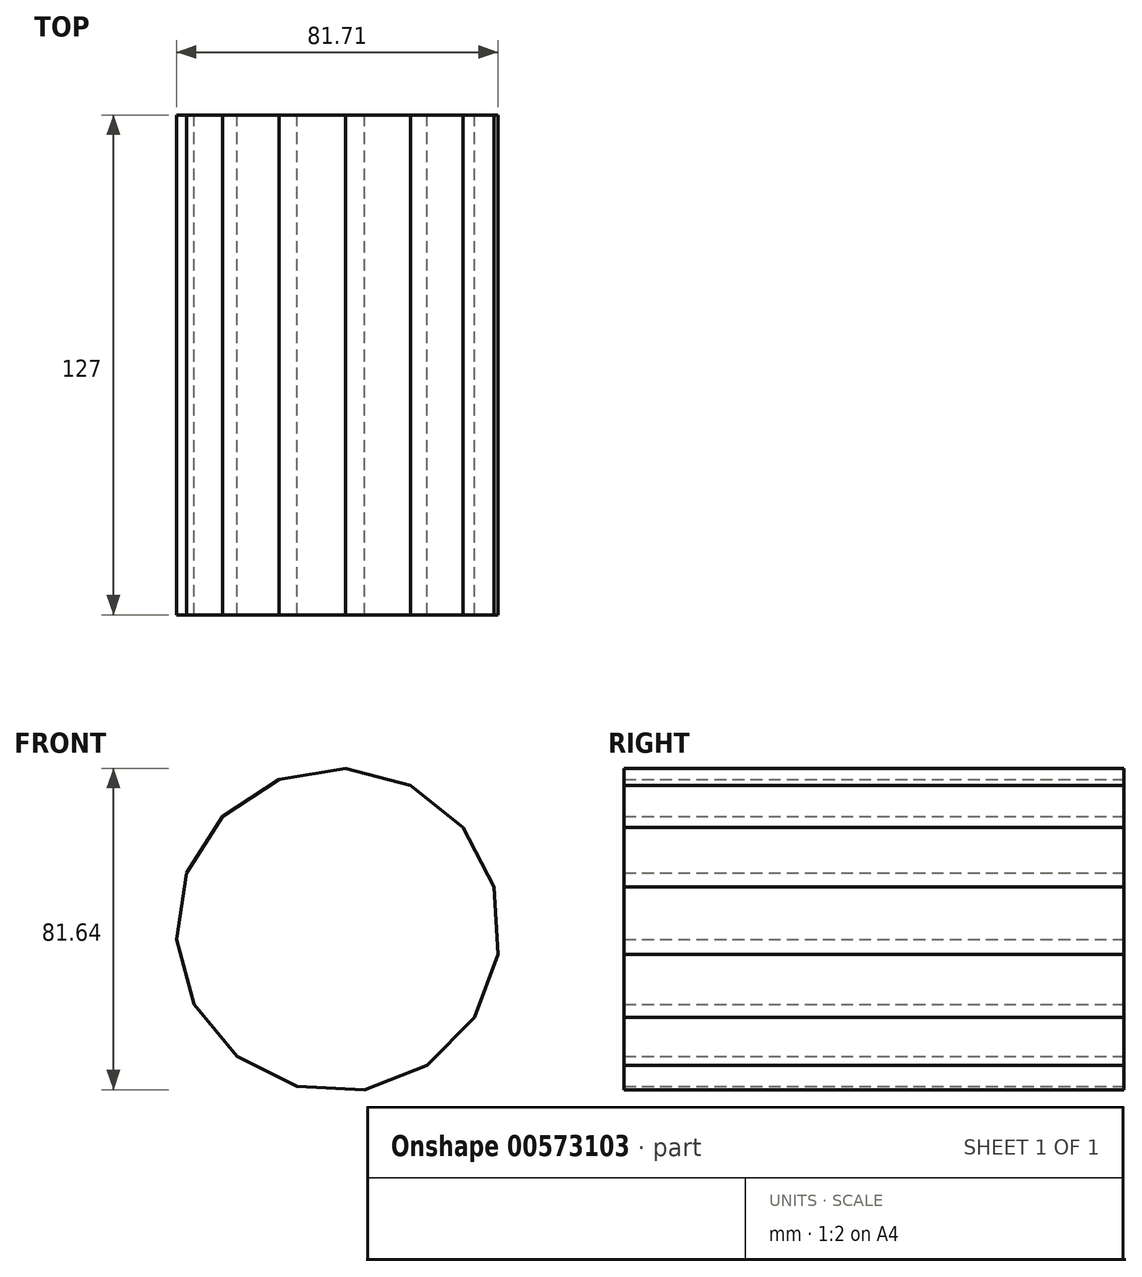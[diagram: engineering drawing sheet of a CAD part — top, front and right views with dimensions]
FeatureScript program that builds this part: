
annotation { "Feature Type Name" : "Feature", "Feature Type Description" : "" }
export const myFeature = defineFeature(function(context is Context, id is Id, definition is map)
    precondition{}
    {
        {
            var Q0;
            Q0=qCreatedBy(makeId("Front.planeOp"),FACE);
            var sketch = newSketch(context, id + "F0", { "sketchPlane" : qUnion([Q0])});
            skCircle(sketch, "E0.cCircle", {"center": v(-0.12, -0.11) * mm, "radius": 40.22 * mm, "construction": true});
            skLineSegment(sketch, "E0.0", {"start": v(34.51, -22.28) * mm, "end": v(22.5, -34.45) * mm});
            skLineSegment(sketch, "E0.1", {"start": v(22.5, -34.45) * mm, "end": v(6.58, -40.68) * mm});
            skLineSegment(sketch, "E0.2", {"start": v(6.58, -40.68) * mm, "end": v(-10.5, -39.9) * mm});
            skLineSegment(sketch, "E0.3", {"start": v(-10.5, -39.9) * mm, "end": v(-25.78, -32.24) * mm});
            skLineSegment(sketch, "E0.4", {"start": v(-25.78, -32.24) * mm, "end": v(-36.63, -19.03) * mm});
            skLineSegment(sketch, "E0.5", {"start": v(-36.63, -19.03) * mm, "end": v(-41.17, -2.54) * mm});
            skLineSegment(sketch, "E0.6", {"start": v(-41.17, -2.54) * mm, "end": v(-38.6, 14.36) * mm});
            skLineSegment(sketch, "E0.7", {"start": v(-38.6, 14.36) * mm, "end": v(-29.39, 28.77) * mm});
            skLineSegment(sketch, "E0.8", {"start": v(-29.39, 28.77) * mm, "end": v(-15.11, 38.17) * mm});
            skLineSegment(sketch, "E0.9", {"start": v(-15.11, 38.17) * mm, "end": v(1.76, 40.96) * mm});
            skLineSegment(sketch, "E0.10", {"start": v(1.76, 40.96) * mm, "end": v(18.3, 36.65) * mm});
            skLineSegment(sketch, "E0.11", {"start": v(18.3, 36.65) * mm, "end": v(31.66, 25.97) * mm});
            skLineSegment(sketch, "E0.12", {"start": v(31.66, 25.97) * mm, "end": v(39.53, 10.8) * mm});
            skLineSegment(sketch, "E0.13", {"start": v(39.53, 10.8) * mm, "end": v(40.54, -6.28) * mm});
            skLineSegment(sketch, "E0.14", {"start": v(40.54, -6.28) * mm, "end": v(34.51, -22.28) * mm});
            skPoint(sketch, "E0.0.midPoint", {"position": v(28.5, -28.36) * mm});
            skSolve(sketch);
        }
        {
            var Q0;
            Q0=makeQuery(id+"F0.imprint","IMPRINT",FACE,{"disambiguationData":[TD([[makeQuery(id+"F0.imprint","IMPRINT",EDGE,{"derivedFrom":sQuery(id+"F0.wireOp",EDGE,"E0.0")}),-1.0]])]});
            extrude(context, id + "F1", {"entities" : qUnion([Q0]), "depth" : 127 * mm, "offsetDistance" : 25.4 * mm});
        }
    });
